# Revit family: BE_51009.2_de_DE
name_source: partatom
category: Leuchten
units: mm (PartAtom-declared; Revit-internal decimal feet)

## family parameters
Basisbauteil = Fläche
Beim Laden mit Abzugskörper schneiden = Ja
Bemaßung runder Anschluss = Durchmesser verwenden
Gemeinsam genutzt = Nein
Lichtquelle = Nein
Raumberechnungspunkt = Ja
Teiletyp = Normal

## types (1)
- BEGA_51009.2_K3
    Aktualisierung = 2023-06-26T04:00:04
    BEGA_Dummy = Nein
    BEGA_Intern = Ja
    Beschreibung = Systempendelleuchte
    Beschreibung_Sonderanfertigung = Hier können Sie Informationen zur Sonderanfertigung eintragen.
    Bestellnummer = 51009.2K3
    CE_Konformität = ja
    ENEC = ja
    Energieeffizienzklasse = LED A++ - A
    Farbtemperatur = 3000 K
    Farbwiedergabeindex = CRI > 90
    Gewicht = 1.4 kg
    Hersteller = BEGA
    LED_Modulbezeichnung = LED-0978/930
    Lampe = LED 16.8 W
    Lampenlichtstrom = 2440 lm
    Lastklassifizierung = Beleuchtung
    Lebensdauerkriterien = L70B50 @ 25 °C = 200000 h
    Leuchtenlichtstrom = 1660 lm
    Logo = BEGA_Logo.png
    Material_15 = BEGA_Leuchtmedium_matt
    Material_17 = BEGA_Reflektor
    Material_18 = BEGA_Gummi_schwarz
    Material_19 = BEGA_Dummy_matt
    Material_22 = BEGA_Oberfläche_Aluminium_matt
    Material_23 = BEGA_Oberfläche_Chrom_poliert
    Material_35 = BEGA_Oberfläche_Samtschwarz_matt
    Modell = 51009.2K3
    Produktdatenblatt = https://cdn.bega.com
    Scheinlast = 0 VA
    Schutzart = IP 20
    Schutzklasse = III
    Sonderanfertigung = Nein
    Spannung = 240 V
    URL = https://www.bega.com
    Umgebungstemperatur = 25 °C
    Vorgabe-Ansicht = 0 mm  [stored 0 ft]

note: [stored X ft] marks values corroborated as IEEE doubles in the binary element streams (Revit-internal decimal feet)

## geometry (parser evidence)
native form markers: Blend x7
no freeform markers — native parametric forms only
